# Revit family: Stainless_Steel_16_Gauge_Mop_Sink-Elkay-FLR-1X
name_source: partatom
category: Plumbing Fixtures
units: mm (PartAtom-declared; Revit-internal decimal feet)

## family parameters
Always vertical = Yes
Cut with Voids When Loaded = No
Maintain Annotation Orientation = No
OmniClass Number = 23.45.05.14.14
OmniClass Title = Sinks/Lavatories
Part Type = Normal
Room Calculation Point = No
Round Connector Dimension = Use Diameter
Shared = No
Work Plane-Based = No

## types (1)
- FLR-1X (16 Gauge Mop Sink)
    Approx.Shipping Weight (Ibs) = 28
    Assembly Code = D2010440
    Bowl Depth = 6.000"
    Bowl Dimesions = 20 inch X 16 inch X 6 inch
    Bowl Length = 20.000"
    Bowl Width = 16.000"
    Default Elevation = 0.000"
    Depth = 11.400"
    Description = Stainless Steel 24 inch X 20 inch X 11 1/4 inch 16 Gauge Mop Sink
    Drain Length From Bowl = 10.000"
    Drain Location = Center
    Drain Width From Bowl = 8.000"
    Edge Height = 1.500"
    Gauge = 16
    Installation Type = Floor Mount
    Length = 24.000"
    Main Material = Finish-Elkay-Stainless Steel
    Manufacturer = Elkay Manufracturer Company
    Manufacturer Brand = Elkay (by Zurn Water solution)
    Model = FLR-1X
    No of Bowls = 1
    Outlet connection Size (inch) = 1.500"
    Product Documentation Link = https://www.elkayfiles.com
    Product Installation Sheet URL = https://www.elkayfiles.com
    Product Page URL = https://www.elkay.com
    Product Weight (lbs) = 25
    Product data URL = https://www.bimobject.com
    Radius for mask = 0.750"
    Repair Parts URL = https://www.elkayfiles.com
    Sink Dimensions = 24 inch X 20 inch X 11 1/4 inch
    Skirt Depth = 10.000"
    URL = https://www.elkay.com
    Width = 20.000"

## geometry (parser evidence)
native form markers: Sweep x2
no freeform markers — native parametric forms only
